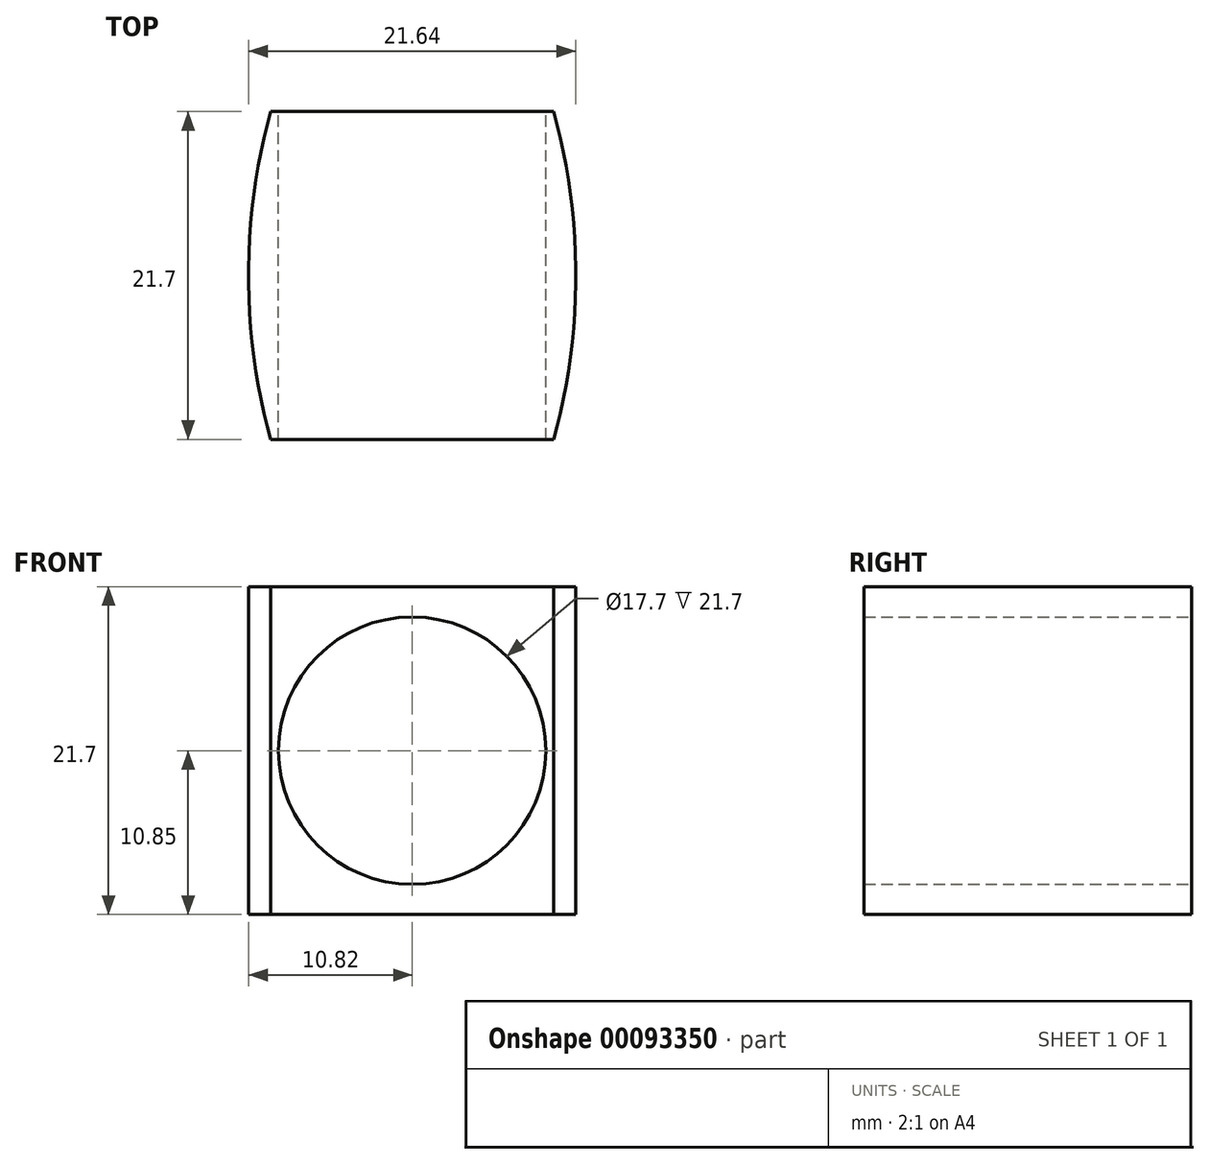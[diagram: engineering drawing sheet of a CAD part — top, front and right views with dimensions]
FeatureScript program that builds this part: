
annotation { "Feature Type Name" : "Feature", "Feature Type Description" : "" }
export const myFeature = defineFeature(function(context is Context, id is Id, definition is map)
    precondition{}
    {
        {
            var Q0;
            Q0=qCreatedBy(makeId("Front.planeOp"),FACE);
            var sketch = newSketch(context, id + "F0", { "sketchPlane" : qUnion([Q0])});
            skLineSegment(sketch, "E0.bottom", {"start": v(8.85, -8.85) * mm, "end": v(-8.85, -8.85) * mm, "construction": true});
            skLineSegment(sketch, "E0.top", {"start": v(8.85, 8.85) * mm, "end": v(-8.85, 8.85) * mm, "construction": true});
            skLineSegment(sketch, "E0.left", {"start": v(8.85, -8.85) * mm, "end": v(8.85, 8.85) * mm, "construction": true});
            skLineSegment(sketch, "E0.right", {"start": v(-8.85, -8.85) * mm, "end": v(-8.85, 8.85) * mm, "construction": true});
            skPoint(sketch, "E0.middle", {"position": v(0, 0) * mm});
            skCircle(sketch, "E1", {"center": v(0, 0) * mm, "radius": 8.85 * mm});
            skLineSegment(sketch, "E2.0", {"start": v(10.85, 10.85) * mm, "end": v(-10.85, 10.85) * mm});
            skLineSegment(sketch, "E2.1", {"start": v(10.85, -10.85) * mm, "end": v(10.85, 10.85) * mm});
            skLineSegment(sketch, "E2.2", {"start": v(10.85, -10.85) * mm, "end": v(-10.85, -10.85) * mm});
            skLineSegment(sketch, "E2.3", {"start": v(-10.85, -10.85) * mm, "end": v(-10.85, 10.85) * mm});
            skSolve(sketch);
        }
        {
            var Q0;
            Q0=makeQuery(id+"F0.imprint","IMPRINT",FACE,{"disambiguationData":[TD([[makeQuery(id+"F0.imprint","IMPRINT",EDGE,{"derivedFrom":sQuery(id+"F0.wireOp",EDGE,"E1")}),-1.0]])]});
            extrude(context, id + "F1", {"entities" : qUnion([Q0]), "depth" : (21.7 / 2) * mm, "hasSecondDirection" : true, "secondDirectionOppositeDirection" : true, "secondDirectionDepth" : 10.85 * mm});
        }
        {
            var Q0;
            Q0=makeQuery(id+"F1.opExtrude","SWEPT_FACE",FACE,{"disambiguationData":[OSD([sQuery(id+"F0.wireOp",EDGE,"E2.0")])]});
            var sketch = newSketch(context, id + "F2", { "sketchPlane" : qUnion([Q0])});
            skEllipse(sketch, "E3", {"center": v(0, 0) * mm, "majorRadius": 21.58 * mm, "minorRadius": 10.82 * mm, "majorAxis": v(0, -1)});
            skLineSegment(sketch, "E4", {"start": v(8.72, 12.78) * mm, "end": v(17.92, 12.78) * mm});
            skLineSegment(sketch, "E5", {"start": v(17.92, 12.78) * mm, "end": v(17.92, -14.68) * mm});
            skLineSegment(sketch, "E6", {"start": v(17.92, -14.68) * mm, "end": v(7.94, -14.68) * mm});
            skLineSegment(sketch, "E7.MirrorCS", {"start": v(-8.72, 12.78) * mm, "end": v(-17.92, 12.78) * mm});
            skLineSegment(sketch, "E8.MirrorCS", {"start": v(-17.92, 12.78) * mm, "end": v(-17.92, -14.68) * mm});
            skLineSegment(sketch, "E9.MirrorCS", {"start": v(-17.92, -14.68) * mm, "end": v(-7.94, -14.68) * mm});
            skSolve(sketch);
        }
        {
            var Q0;
            {var subQ0=sQuery(id+"F2.wireOp",EDGE,"E4");Q0=makeQuery(id+"F2.imprint","IMPRINT",FACE,{"disambiguationData":[TD([[makeQuery(id+"F2.imprint","IMPRINT",EDGE,{"derivedFrom":subQ0}),-1.0]])]});}
            var Q1;
            {var subQ0=sQuery(id+"F2.wireOp",EDGE,"E7.MirrorCS");Q1=makeQuery(id+"F2.imprint","IMPRINT",FACE,{"disambiguationData":[TD([[makeQuery(id+"F2.imprint","IMPRINT",EDGE,{"derivedFrom":subQ0}),1.0]])]});}
            var Q2;
            {var subQ1=sQuery(id+"F0.wireOp",EDGE,"E2.0");var subQ6=makeQuery(id+"F1.opExtrude","SWEPT_EDGE",EDGE,{"disambiguationData":[OSD([subQ1,sQuery(id+"F0.wireOp",EDGE,"E2.1")])]});Q2=makeQuery(id+"F2.imprint","IMPRINT",FACE,{"disambiguationData":[TD([[makeQuery(id+"F2.imprint","IMPRINT",EDGE,{"derivedFrom":subQ6}),1.0]])]});}
            var Q3;
            {var subQ1=sQuery(id+"F0.wireOp",EDGE,"E2.0");var subQ6=makeQuery(id+"F1.opExtrude","SWEPT_EDGE",EDGE,{"disambiguationData":[OSD([subQ1,sQuery(id+"F0.wireOp",EDGE,"E2.3")])]});Q3=makeQuery(id+"F2.imprint","IMPRINT",FACE,{"disambiguationData":[TD([[makeQuery(id+"F2.imprint","IMPRINT",EDGE,{"derivedFrom":subQ6}),-1.0]])]});}
            extrude(context, id + "F3", {"entities" : qUnion([Q0, Q1, Q2, Q3]), "operationType" : NewBodyOperationType.REMOVE, "oppositeDirection" : true, "depth" : 25 * mm});
        }
    });
